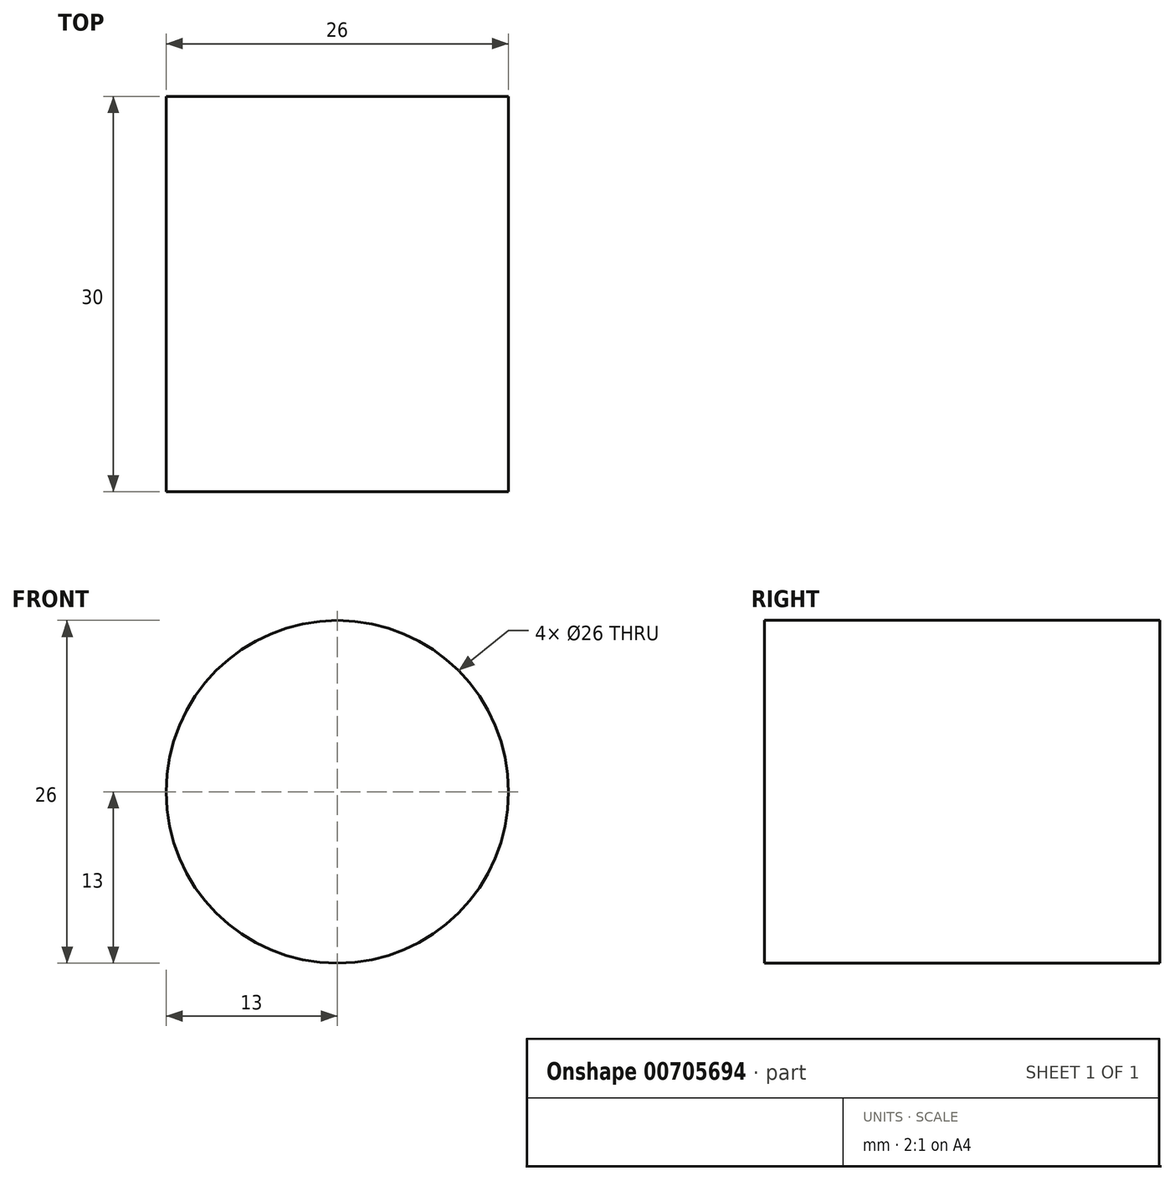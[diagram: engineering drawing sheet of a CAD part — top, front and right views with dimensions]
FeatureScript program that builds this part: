
annotation { "Feature Type Name" : "Feature", "Feature Type Description" : "" }
export const myFeature = defineFeature(function(context is Context, id is Id, definition is map)
    precondition{}
    {
        {
            var Q0;
            Q0=qCreatedBy(makeId("Front.planeOp"),FACE);
            var sketch = newSketch(context, id + "F0", { "sketchPlane" : qUnion([Q0])});
            skCircle(sketch, "E0", {"center": v(0, 0) * mm, "radius": 13 * mm});
            skCircle(sketch, "E1", {"center": v(0, 0) * mm, "radius": 3 * mm});
            skSolve(sketch);
        }
        {
            var Q0;
            Q0=sQuery(id+"F0.wireOp",EDGE,"E0");
            extrude(context, id + "F1", {"bodyType" : ToolBodyType.SURFACE, "surfaceEntities" : qUnion([Q0]), "oppositeDirection" : true, "depth" : 30 * mm, "offsetDistance" : 25 * mm});
        }
    });
